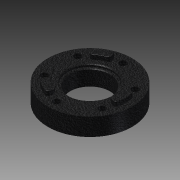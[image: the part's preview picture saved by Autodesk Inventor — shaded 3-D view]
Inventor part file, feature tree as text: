
AUTODESK INVENTOR PART (.ipt)
format: ipt  version: 2014 SP1 (Build 180222100, 222)  size: 2,207,744 bytes
history: native  units: in
note: dims shown in document units (in); Inventor stores cm internally (conversion verified against a paired STEP export)
features: extrude x10, sketch x10, pattern_circular x1, plane x1, imported_body x1
ambient origin geometry x8: Origin, YZ Plane, XZ Plane, XY Plane, X Axis, Y Axis, Z Axis, Center Point
bodies: Body1 (feature_tree)
feature tree (23):
  pattern_circular  "CirPattern2"
  extrude  "Extrusion1"  Depth=0.5in TaperAngle=0.0deg
  extrude  "Extrusion2"  Depth=0.5in TaperAngle=0.0deg
  plane  "Work Plane1"
  extrude  "Extrusion3"  Depth=0.2in
  extrude  "Extrusion4"  Depth=0.2in
  extrude  "Extrusion5"  Depth=0.2in
  extrude  "Extrusion6"  Depth=1.0in TaperAngle=0.0deg
  extrude  "Extrusion7"  Depth=0.5in
  extrude  "Extrusion8"  Depth=0.5in TaperAngle=0.0deg
  extrude  "Extrusion9"  Depth=0.5in TaperAngle=0.0deg
  extrude  "Extrusion10"  [1 undecoded]
  imported_body  "Base1"
  sketch  "Sketch1"  dims[d0=0.5in d1=0.0in d2=0.0002in d3=0.0in]
  sketch  "Sketch2"  dims[d4=-0.25in d5=0.5in d6=0.0in]
  sketch  "Sketch4"  dims[d7=0.25in d8=0.0in d9=0.2in]
  sketch  "Sketch5"  dims[d10=2.3622in d12=0.0in d14=0.2in]
  sketch  "Sketch6"  dims[d15=0.2in d16=0.2in]
  sketch  "Sketch7"  dims[d17=0.2in d18=1.0in d19=0.0in]
  sketch  "Sketch8"  dims[d20=0.5in d21=0.0in d22=2.375in]
  sketch  "Sketch10"  dims[d23=0.5in d24=0.0in d25=0.5in d26=0.0in]
  sketch  "Sketch11"  dims[d27=0.5in d28=0.0in d29=0.5in d30=0.0in]
  sketch  "Sketch12"
note: 1 required parameter value undecoded (feature->parameter linkage not recoverable at this tier; creation-order binding heuristic only, values carry confidence <= 0.55)
